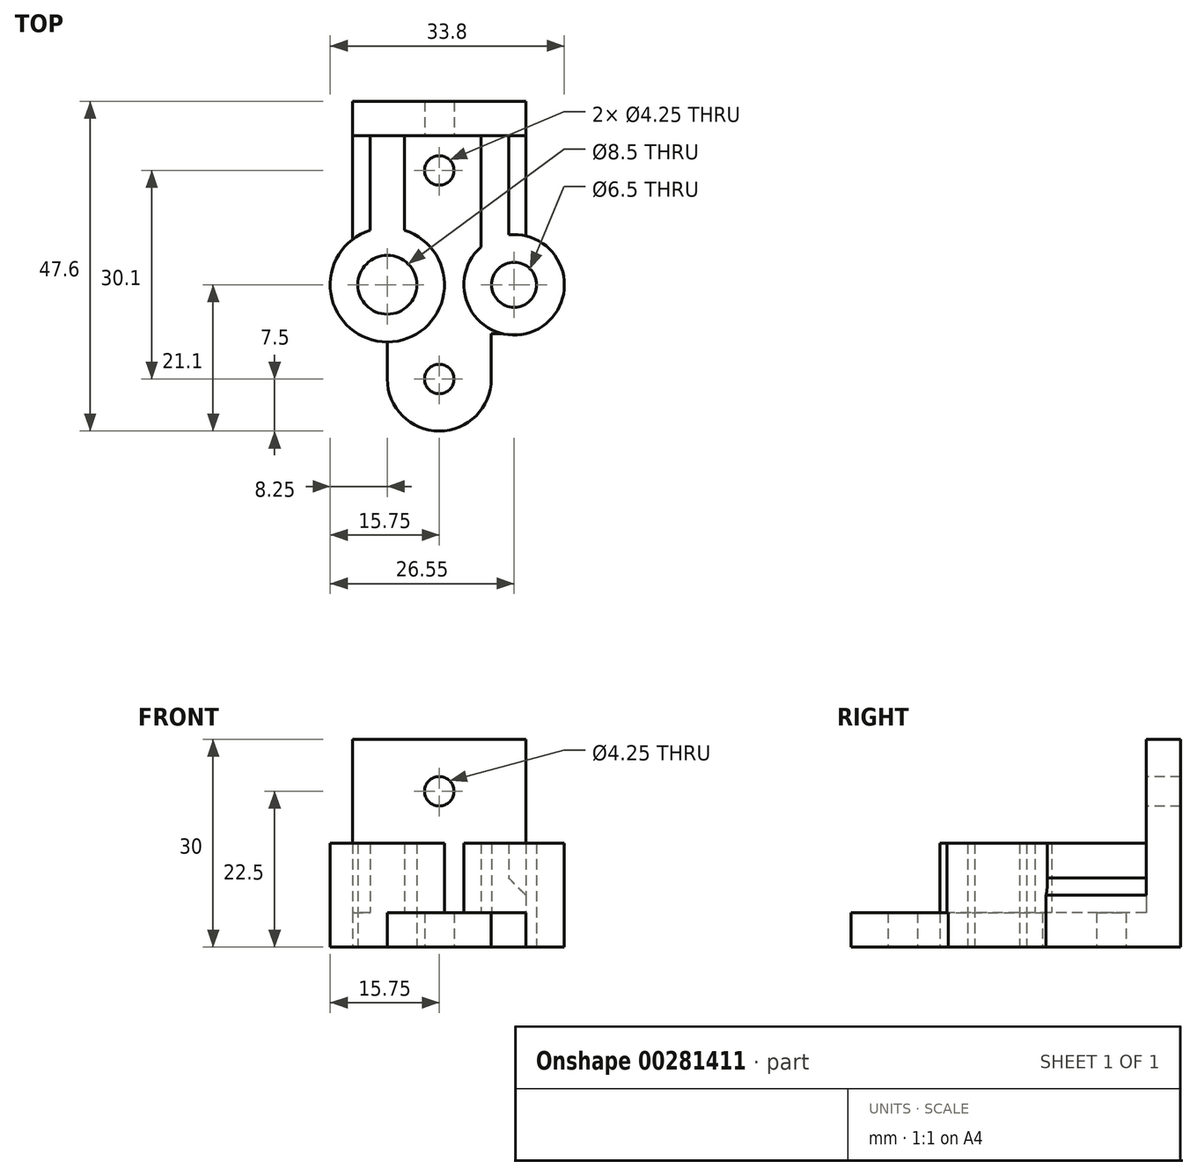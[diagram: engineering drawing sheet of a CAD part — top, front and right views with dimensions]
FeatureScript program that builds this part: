
annotation { "Feature Type Name" : "Feature", "Feature Type Description" : "" }
export const myFeature = defineFeature(function(context is Context, id is Id, definition is map)
    precondition{}
    {
        {
            var Q0;
            Q0=qCreatedBy(makeId("Top.planeOp"),FACE);
            var sketch = newSketch(context, id + "F0", { "sketchPlane" : qUnion([Q0])});
            skLineSegment(sketch, "E0", {"start": v(0, 26.5) * mm, "end": v(12.5, 26.5) * mm});
            skLineSegment(sketch, "E1", {"start": v(12.5, 26.5) * mm, "end": v(12.5, 7.05) * mm});
            skLineSegment(sketch, "E2", {"start": v(0, -21.1) * mm, "end": v(0, -21.1) * mm});
            skCircle(sketch, "E3", {"center": v(0, 16.5) * mm, "radius": 2.12 * mm});
            skCircle(sketch, "E4", {"center": v(0, -13.6) * mm, "radius": 2.12 * mm});
            skCircle(sketch, "E5", {"center": v(-7.5, 0) * mm, "radius": 4.25 * mm});
            skCircle(sketch, "E6", {"center": v(10.8, 0) * mm, "radius": 3.25 * mm});
            skLineSegment(sketch, "E7.MirrorCS", {"start": v(0, 26.5) * mm, "end": v(-12.5, 26.5) * mm});
            skLineSegment(sketch, "E8.MirrorCS", {"start": v(-12.5, 26.5) * mm, "end": v(-12.5, 6.56) * mm});
            skLineSegment(sketch, "E9", {"start": v(7.5, -13.6) * mm, "end": v(7.5, -7.05) * mm});
            skLineSegment(sketch, "E10", {"start": v(7.5, -7.05) * mm, "end": v(12.5, -7.05) * mm});
            skLineSegment(sketch, "E11", {"start": v(-7.5, -8.25) * mm, "end": v(-7.5, -13.6) * mm});
            skArc(sketch, "E12", {"start": v(-7.5, -8.25) * mm, "mid": v(-15.32, -2.64) * mm, "end": v(-12.5, 6.56) * mm});
            skArc(sketch, "E13", {"start": v(12.5, 7.05) * mm, "mid": v(18.05, 0) * mm, "end": v(12.5, -7.05) * mm});
            skPoint(sketch, "E14.trimOffspring.end.orphan", {"position": v(-12.5, -21.1) * mm});
            skPoint(sketch, "E15.orphan", {"position": v(12.5, -21.1) * mm});
            skPoint(sketch, "E16.visualSharp", {"position": v(-7.5, -21.1) * mm});
            skArc(sketch, "E16.filletArc", {"start": v(-7.5, -13.6) * mm, "mid": v(-5.3, -18.9) * mm, "end": v(0, -21.1) * mm});
            skPoint(sketch, "E17.visualSharp", {"position": v(7.5, -21.1) * mm});
            skArc(sketch, "E17.filletArc", {"start": v(0, -21.1) * mm, "mid": v(5.3, -18.9) * mm, "end": v(7.5, -13.6) * mm});
            skSolve(sketch);
        }
        {
            var Q0;
            Q0=qSketchRegion(id+"F0",true);
            extrude(context, id + "F1", {"entities" : qUnion([Q0]), "depth" : 5 * mm});
        }
        {
            var Q0;
            Q0=makeQuery(id+"F1.opExtrude","CAP_FACE",FACE,{"disambiguationData":[OSD([sQuery(id+"F0.wireOp",EDGE,"E0"),sQuery(id+"F0.wireOp",EDGE,"E1"),sQuery(id+"F0.wireOp",EDGE,"E2"),sQuery(id+"F0.wireOp",EDGE,"E3"),sQuery(id+"F0.wireOp",EDGE,"E4"),sQuery(id+"F0.wireOp",EDGE,"E5"),sQuery(id+"F0.wireOp",EDGE,"E6"),sQuery(id+"F0.wireOp",EDGE,"E7.MirrorCS"),sQuery(id+"F0.wireOp",EDGE,"E8.MirrorCS"),sQuery(id+"F0.wireOp",EDGE,"E2"),sQuery(id+"F0.wireOp",EDGE,"E9"),sQuery(id+"F0.wireOp",EDGE,"E10"),sQuery(id+"F0.wireOp",EDGE,"E11"),sQuery(id+"F0.wireOp",EDGE,"E12"),sQuery(id+"F0.wireOp",EDGE,"E13")])],"isStart":false});
            var sketch = newSketch(context, id + "F2", { "sketchPlane" : qUnion([Q0])});
            skLineSegment(sketch, "E18.bottom", {"start": v(-12.5, 26.5) * mm, "end": v(12.5, 26.5) * mm});
            skLineSegment(sketch, "E18.top", {"start": v(-12.5, 21.5) * mm, "end": v(12.5, 21.5) * mm});
            skLineSegment(sketch, "E18.left", {"start": v(-12.5, 26.5) * mm, "end": v(-12.5, 21.5) * mm});
            skLineSegment(sketch, "E18.right", {"start": v(12.5, 26.5) * mm, "end": v(12.5, 21.5) * mm});
            skSolve(sketch);
        }
        {
            var Q0;
            Q0=qSketchRegion(id+"F2",true);
            extrude(context, id + "F3", {"entities" : qUnion([Q0]), "operationType" : NewBodyOperationType.ADD, "depth" : 25 * mm});
        }
        {
            var Q0;
            Q0=makeQuery(id+"F1.opExtrude","CAP_FACE",FACE,{"disambiguationData":[OSD([sQuery(id+"F0.wireOp",EDGE,"E0"),sQuery(id+"F0.wireOp",EDGE,"E1"),sQuery(id+"F0.wireOp",EDGE,"E3"),sQuery(id+"F0.wireOp",EDGE,"E4"),sQuery(id+"F0.wireOp",EDGE,"E5"),sQuery(id+"F0.wireOp",EDGE,"E6"),sQuery(id+"F0.wireOp",EDGE,"E7.MirrorCS"),sQuery(id+"F0.wireOp",EDGE,"E8.MirrorCS"),sQuery(id+"F0.wireOp",EDGE,"E9"),sQuery(id+"F0.wireOp",EDGE,"E10"),sQuery(id+"F0.wireOp",EDGE,"E11"),sQuery(id+"F0.wireOp",EDGE,"E12"),sQuery(id+"F0.wireOp",EDGE,"E13"),sQuery(id+"F0.wireOp",EDGE,"E16.filletArc"),sQuery(id+"F0.wireOp",EDGE,"E17.filletArc")])],"isStart":false});
            var sketch = newSketch(context, id + "F4", { "sketchPlane" : qUnion([Q0])});
            skCircle(sketch, "E19", {"center": v(-7.5, 0) * mm, "radius": 4.25 * mm});
            skCircle(sketch, "E20", {"center": v(-7.5, 0) * mm, "radius": 8.25 * mm});
            skCircle(sketch, "E21", {"center": v(10.8, 0) * mm, "radius": 3.25 * mm});
            skCircle(sketch, "E22", {"center": v(10.8, 0) * mm, "radius": 7.25 * mm});
            skSolve(sketch);
        }
        {
            var Q0;
            Q0=qSketchRegion(id+"F4",true);
            extrude(context, id + "F5", {"entities" : qUnion([Q0]), "operationType" : NewBodyOperationType.ADD, "depth" : 10 * mm});
        }
        {
            var Q0;
            Q0=makeQuery(id+"F3.opExtrude","SWEPT_FACE",FACE,{"disambiguationData":[OSD([sQuery(id+"F2.wireOp",EDGE,"E18.top")])]});
            var sketch = newSketch(context, id + "F6", { "sketchPlane" : qUnion([Q0])});
            skCircle(sketch, "E23", {"center": v(0, 22.5) * mm, "radius": 2.12 * mm});
            skSolve(sketch);
        }
        {
            var Q0;
            Q0=qSketchRegion(id+"F6",true);
            extrude(context, id + "F7", {"entities" : qUnion([Q0]), "operationType" : NewBodyOperationType.REMOVE, "endBound" : BoundingType.THROUGH_ALL, "oppositeDirection" : true, "depth" : 25 * mm});
        }
        {
            var Q0;
            Q0=makeQuery(id+"F1.opExtrude","CAP_FACE",FACE,{"disambiguationData":[OSD([sQuery(id+"F0.wireOp",EDGE,"E0"),sQuery(id+"F0.wireOp",EDGE,"E1"),sQuery(id+"F0.wireOp",EDGE,"E3"),sQuery(id+"F0.wireOp",EDGE,"E4"),sQuery(id+"F0.wireOp",EDGE,"E5"),sQuery(id+"F0.wireOp",EDGE,"E6"),sQuery(id+"F0.wireOp",EDGE,"E7.MirrorCS"),sQuery(id+"F0.wireOp",EDGE,"E8.MirrorCS"),sQuery(id+"F0.wireOp",EDGE,"E9"),sQuery(id+"F0.wireOp",EDGE,"E10"),sQuery(id+"F0.wireOp",EDGE,"E11"),sQuery(id+"F0.wireOp",EDGE,"E12"),sQuery(id+"F0.wireOp",EDGE,"E13"),sQuery(id+"F0.wireOp",EDGE,"E16.filletArc"),sQuery(id+"F0.wireOp",EDGE,"E17.filletArc")])],"isStart":false});
            var sketch = newSketch(context, id + "F8", { "sketchPlane" : qUnion([Q0])});
            skLineSegment(sketch, "E24.bottom", {"start": v(-10, 21.5) * mm, "end": v(-5, 21.5) * mm});
            skLineSegment(sketch, "E24.top", {"start": v(-10, 7.86) * mm, "end": v(-5, 7.86) * mm});
            skLineSegment(sketch, "E24.left", {"start": v(-10, 21.5) * mm, "end": v(-10, 7.86) * mm});
            skLineSegment(sketch, "E24.right", {"start": v(-5, 21.5) * mm, "end": v(-5, 7.86) * mm});
            skLineSegment(sketch, "E25.bottom", {"start": v(6, 21.5) * mm, "end": v(10, 21.5) * mm});
            skLineSegment(sketch, "E25.top", {"start": v(6, 5.43) * mm, "end": v(10, 5.43) * mm});
            skLineSegment(sketch, "E25.left", {"start": v(6, 21.5) * mm, "end": v(6, 5.43) * mm});
            skLineSegment(sketch, "E25.right", {"start": v(10, 21.5) * mm, "end": v(10, 5.43) * mm});
            skSolve(sketch);
        }
        {
            var Q0;
            Q0=qSketchRegion(id+"F8",true);
            extrude(context, id + "F9", {"entities" : qUnion([Q0]), "operationType" : NewBodyOperationType.ADD, "depth" : 10 * mm});
        }
        {
            var Q0;
            Q0=makeQuery(id+"F9.opExtrude","CAP_EDGE",EDGE,{"disambiguationData":[OSD([sQuery(id+"F8.wireOp",EDGE,"E24.bottom")])],"isStart":false});
            var Q1;
            Q1=makeQuery(id+"F9.opExtrude","CAP_EDGE",EDGE,{"disambiguationData":[OSD([sQuery(id+"F8.wireOp",EDGE,"E25.bottom")])],"isStart":false});
            var Q2;
            Q2=makeQuery(id+"F9.opExtrude","CAP_EDGE",EDGE,{"disambiguationData":[OSD([sQuery(id+"F8.wireOp",EDGE,"E24.left")])],"isStart":true});
            var Q3;
            Q3=makeQuery(id+"F9.opExtrude","CAP_EDGE",EDGE,{"disambiguationData":[OSD([sQuery(id+"F8.wireOp",EDGE,"E25.right")])],"isStart":true});
            chamfer(context, id + "F10", {"entities" : qUnion([Q0, Q1, Q2, Q3]), "width" : 5 * mm, "tangentPropagation" : true});
        }
    });
